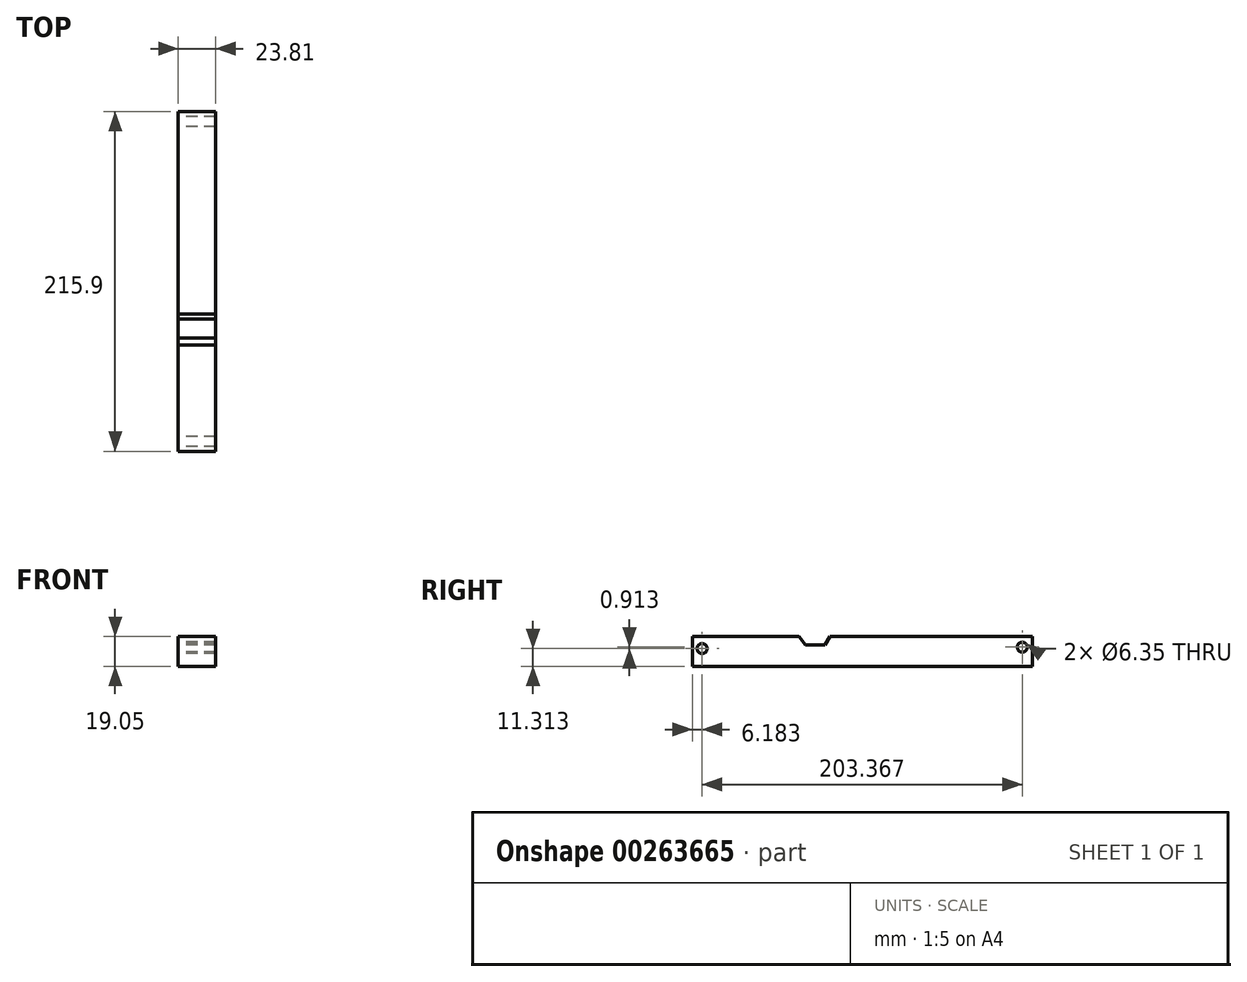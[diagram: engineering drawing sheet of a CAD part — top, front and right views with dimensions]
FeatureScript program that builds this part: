
annotation { "Feature Type Name" : "Feature", "Feature Type Description" : "" }
export const myFeature = defineFeature(function(context is Context, id is Id, definition is map)
    precondition{}
    {
        {
            var Q0;
            Q0=qCreatedBy(makeId("Front.planeOp"),FACE);
            var sketch = newSketch(context, id + "F0", { "sketchPlane" : qUnion([Q0])});
            skLineSegment(sketch, "E0.bottom", {"start": v(0, 0) * mm, "end": v(23.81, 0) * mm});
            skLineSegment(sketch, "E0.top", {"start": v(0, 19.05) * mm, "end": v(23.81, 19.05) * mm});
            skLineSegment(sketch, "E0.left", {"start": v(0, 0) * mm, "end": v(0, 19.05) * mm});
            skLineSegment(sketch, "E0.right", {"start": v(23.81, 0) * mm, "end": v(23.81, 19.05) * mm});
            skSolve(sketch);
        }
        {
            var Q0;
            Q0=makeQuery(id+"F0.imprint","IMPRINT",FACE,{"disambiguationData":[TD([[makeQuery(id+"F0.imprint","IMPRINT",EDGE,{"derivedFrom":sQuery(id+"F0.wireOp",EDGE,"E0.bottom")}),1.0]])]});
            extrude(context, id + "F1", {"entities" : qUnion([Q0]), "depth" : 215.9 * mm});
        }
        {
            var Q0;
            Q0=qCreatedBy(makeId("Right.planeOp"),FACE);
            var sketch = newSketch(context, id + "F2", { "sketchPlane" : qUnion([Q0])});
            skLineSegment(sketch, "E1", {"start": v(-152.03, 23.8) * mm, "end": v(-144.04, 13.76) * mm});
            skLineSegment(sketch, "E2", {"start": v(-144.04, 13.76) * mm, "end": v(-131.7, 13.76) * mm});
            skLineSegment(sketch, "E3", {"start": v(-131.7, 13.76) * mm, "end": v(-125.7, 23.73) * mm});
            skLineSegment(sketch, "E4", {"start": v(-125.7, 23.73) * mm, "end": v(-152.03, 23.8) * mm});
            skLineSegment(sketch, "E5", {"start": v(-125.7, 23.73) * mm, "end": v(-130.12, 34.17) * mm});
            skLineSegment(sketch, "E6", {"start": v(-130.12, 34.17) * mm, "end": v(-152.03, 23.8) * mm});
            skSolve(sketch);
        }
        {
            var Q0;
            Q0 = qSketchRegion(id + "F2", true);
            extrude(context, id + "F3", {"entities" : qUnion([Q0]), "operationType" : NewBodyOperationType.REMOVE, "depth" : 25.4 * mm});
        }
        {
            var Q0;
            Q0=qCreatedBy(makeId("Right.planeOp"),FACE);
            var sketch = newSketch(context, id + "F4", { "sketchPlane" : qUnion([Q0])});
            skLineSegment(sketch, "E7", {"start": v(0, 12.23) * mm, "end": v(-6.35, 12.23) * mm});
            skCircle(sketch, "E8", {"center": v(-6.35, 12.23) * mm, "radius": 4.26 * mm});
            skSolve(sketch);
        }
        {
            var Q0;
            Q0=sQuery(id+"F4.wireOp",VERTEX,"E8.center");
            var Q1;
            Q1=makeQuery(id+"F1.opExtrude","SWEPT_BODY",BODY,{"disambiguationData":[OSD([sQuery(id+"F0.wireOp",EDGE,"E0.bottom"),sQuery(id+"F0.wireOp",EDGE,"E0.top"),sQuery(id+"F0.wireOp",EDGE,"E0.left"),sQuery(id+"F0.wireOp",EDGE,"E0.right")])]});
            hole(context, id + "F5", {"style" : HoleStyle.SIMPLE, "endStyle" : HoleEndStyle.BLIND, "oppositeDirection" : true, "holeDiameter" : 6.35 * mm, "holeDepth" : 50.8 * mm, "tappedDepth" : 12.7 * mm, "tapClearance" : 3, "startFromSketch" : true, "locations" : qUnion([Q0]), "scope" : qUnion([Q1])});
        }
        {
            var Q0;
            Q0=qCreatedBy(makeId("Right.planeOp"),FACE);
            var sketch = newSketch(context, id + "F6", { "sketchPlane" : qUnion([Q0])});
            skLineSegment(sketch, "E9", {"start": v(-216.07, 11.31) * mm, "end": v(-209.72, 11.31) * mm});
            skCircle(sketch, "E10", {"center": v(-209.72, 11.31) * mm, "radius": 3.18 * mm});
            skSolve(sketch);
        }
        {
            var Q0;
            Q0=sQuery(id+"F6.wireOp",VERTEX,"E10.center");
            var Q1;
            Q1=makeQuery(id+"F1.opExtrude","SWEPT_BODY",BODY,{"disambiguationData":[OSD([sQuery(id+"F0.wireOp",EDGE,"E0.bottom"),sQuery(id+"F0.wireOp",EDGE,"E0.top"),sQuery(id+"F0.wireOp",EDGE,"E0.left"),sQuery(id+"F0.wireOp",EDGE,"E0.right")])]});
            hole(context, id + "F7", {"style" : HoleStyle.SIMPLE, "endStyle" : HoleEndStyle.BLIND, "oppositeDirection" : true, "holeDiameter" : 6.35 * mm, "holeDepth" : 50.8 * mm, "tappedDepth" : 12.7 * mm, "tapClearance" : 3, "startFromSketch" : true, "locations" : qUnion([Q0]), "scope" : qUnion([Q1])});
        }
    });
